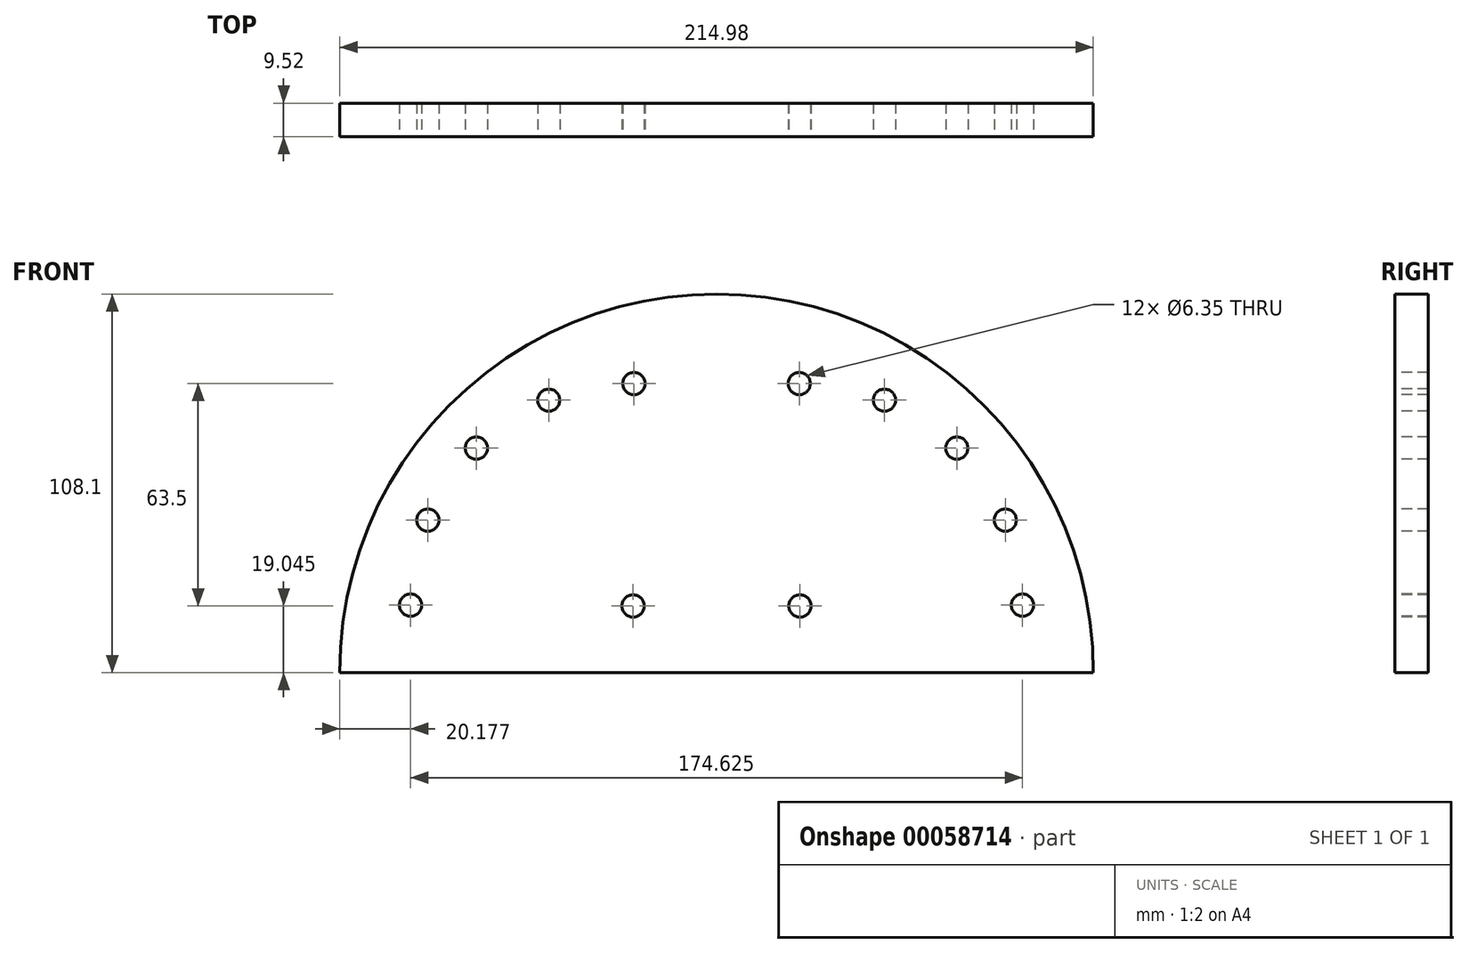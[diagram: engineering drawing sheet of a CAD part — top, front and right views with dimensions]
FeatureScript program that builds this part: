
annotation { "Feature Type Name" : "Feature", "Feature Type Description" : "" }
export const myFeature = defineFeature(function(context is Context, id is Id, definition is map)
    precondition{}
    {
        {
            var Q0;
            Q0=qCreatedBy(makeId("Front.planeOp"),FACE);
            var sketch = newSketch(context, id + "F0", { "sketchPlane" : qUnion([Q0])});
            skLineSegment(sketch, "E0", {"start": v(-107.5, -0.61) * mm, "end": v(108.4, -0.61) * mm});
            skArc(sketch, "E1", {"start": v(-107.5, -0.61) * mm, "mid": v(0, 107.5) * mm, "end": v(107.5, -0.61) * mm});
            skSolve(sketch);
        }
        {
            var Q0;
            Q0=qSketchRegion(id+"F0",true);
            extrude(context, id + "F1", {"entities" : qUnion([Q0]), "endBound" : BoundingType.SYMMETRIC, "depth" : 9.52 * mm});
        }
        {
            var Q0;
            Q0=makeQuery(id+"F1.opExtrude","CAP_FACE",FACE,{"disambiguationData":[OSD([sQuery(id+"F0.wireOp",EDGE,"E0"),sQuery(id+"F0.wireOp",EDGE,"E1")])],"isStart":false});
            var sketch = newSketch(context, id + "F2", { "sketchPlane" : qUnion([Q0])});
            skCircle(sketch, "E2", {"center": v(23.81, 18.44) * mm, "radius": 3.18 * mm});
            skCircle(sketch, "E3", {"center": v(23.59, 81.94) * mm, "radius": 3.18 * mm});
            skCircle(sketch, "E4.1.0", {"center": v(47.9, 77.19) * mm, "radius": 3.18 * mm});
            skCircle(sketch, "E4.2.0", {"center": v(68.55, 63.5) * mm, "radius": 3.18 * mm});
            skLineSegment(sketch, "E4.anchor1", {"start": v(0, 18.44) * mm, "end": v(0, 94.64) * mm, "construction": true});
            skLineSegment(sketch, "E4.anchor2", {"start": v(-4.4, 18.66) * mm, "end": v(87.31, 18.66) * mm, "construction": true});
            skCircle(sketch, "E5.1.3.0", {"center": v(82.4, 42.94) * mm, "radius": 3.18 * mm});
            skCircle(sketch, "E5.1.4.0", {"center": v(87.31, 18.66) * mm, "radius": 3.18 * mm});
            skCircle(sketch, "E6.MirrorC", {"center": v(-23.59, 81.94) * mm, "radius": 3.18 * mm});
            skCircle(sketch, "E7.MirrorC", {"center": v(-47.9, 77.19) * mm, "radius": 3.18 * mm});
            skCircle(sketch, "E8.MirrorC", {"center": v(-68.55, 63.5) * mm, "radius": 3.18 * mm});
            skCircle(sketch, "E9.MirrorC", {"center": v(-82.4, 42.94) * mm, "radius": 3.18 * mm});
            skCircle(sketch, "E10.MirrorC", {"center": v(-87.31, 18.66) * mm, "radius": 3.18 * mm});
            skCircle(sketch, "E11.MirrorC", {"center": v(-23.81, 18.44) * mm, "radius": 3.18 * mm});
            skSolve(sketch);
        }
        {
            var Q0;
            Q0=sQuery(id+"F2.wireOp",VERTEX,"E2.center");
            var Q1;
            Q1=sQuery(id+"F2.wireOp",VERTEX,"E4.anchor2.end");
            var Q2;
            Q2=sQuery(id+"F2.wireOp",VERTEX,"E4.1.0.center");
            var Q3;
            Q3=sQuery(id+"F2.wireOp",VERTEX,"E3.center");
            var Q4;
            Q4=sQuery(id+"F2.wireOp",VERTEX,"E4.2.0.center");
            var Q5;
            Q5=sQuery(id+"F2.wireOp",VERTEX,"E5.1.3.0.center");
            var Q6;
            Q6=sQuery(id+"F2.wireOp",VERTEX,"E11.MirrorC.center");
            var Q7;
            Q7=sQuery(id+"F2.wireOp",VERTEX,"E6.MirrorC.center");
            var Q8;
            Q8=sQuery(id+"F2.wireOp",VERTEX,"E7.MirrorC.center");
            var Q9;
            Q9=sQuery(id+"F2.wireOp",VERTEX,"E8.MirrorC.center");
            var Q10;
            Q10=sQuery(id+"F2.wireOp",VERTEX,"E9.MirrorC.center");
            var Q11;
            Q11=sQuery(id+"F2.wireOp",VERTEX,"E10.MirrorC.center");
            var Q12;
            Q12=makeQuery(id+"F1.opExtrude","SWEPT_BODY",BODY,{"disambiguationData":[OSD([sQuery(id+"F0.wireOp",EDGE,"E0"),sQuery(id+"F0.wireOp",EDGE,"E1")])]});
            hole(context, id + "F3", {"style" : HoleStyle.SIMPLE, "holeDiameter" : 6.35 * mm, "endStyle" : HoleEndStyle.THROUGH, "locations" : qUnion([Q0, Q1, Q2, Q3, Q4, Q5, Q6, Q7, Q8, Q9, Q10, Q11]), "scope" : qUnion([Q12])});
        }
        {
            var Q0;
            Q0=makeQuery(id+"F1.opExtrude","CAP_FACE",FACE,{"disambiguationData":[OSD([sQuery(id+"F0.wireOp",EDGE,"E0"),sQuery(id+"F0.wireOp",EDGE,"E1")])],"isStart":false});
            var sketch = newSketch(context, id + "F4", { "sketchPlane" : qUnion([Q0])});
            skLineSegment(sketch, "E12.bottom", {"start": v(4.76, -8.59) * mm, "end": v(-135.88, -8.59) * mm});
            skLineSegment(sketch, "E12.top", {"start": v(4.76, 118.41) * mm, "end": v(-135.88, 118.41) * mm});
            skLineSegment(sketch, "E13", {"start": v(4.76, 118.41) * mm, "end": v(4.76, -8.59) * mm});
            skLineSegment(sketch, "E14", {"start": v(-135.88, 118.41) * mm, "end": v(-135.88, -8.59) * mm});
            skSolve(sketch);
        }
        {
            var Q0;
            {var subQ1=sQuery(id+"F4.wireOp",EDGE,"E12.bottom");Q0=makeQuery(id+"F4.imprint","IMPRINT",FACE,{"disambiguationData":[TD([[makeQuery(id+"F4.imprint","IMPRINT",EDGE,{"derivedFrom":subQ1}),-1.0]])]});}
            var Q1;
            Q1=makeQuery(id+"F4.imprint","IMPRINT",FACE,{"disambiguationData":[TD([[makeQuery(id+"F4.imprint","IMPRINT",EDGE,{"derivedFrom":makeQuery(id+"F3.hole-6.boolean.opBoolean","COPY",EDGE,{"derivedFrom":makeQuery(id+"F3.hole-6.opRevolve","SWEPT_EDGE",EDGE,{"disambiguationData":[OSD([sQuery(id+"F3.hole-6.sketch.wireOp",EDGE,"core_line_2"),sQuery(id+"F3.hole-6.sketch.wireOp",EDGE,"core_line_3")])]})})}),-1.0]])]});
            extrude(context, id + "F5", {"entities" : qUnion([Q0, Q1]), "operationType" : NewBodyOperationType.REMOVE, "oppositeDirection" : true, "depth" : 25.4 * mm});
        }
    });
